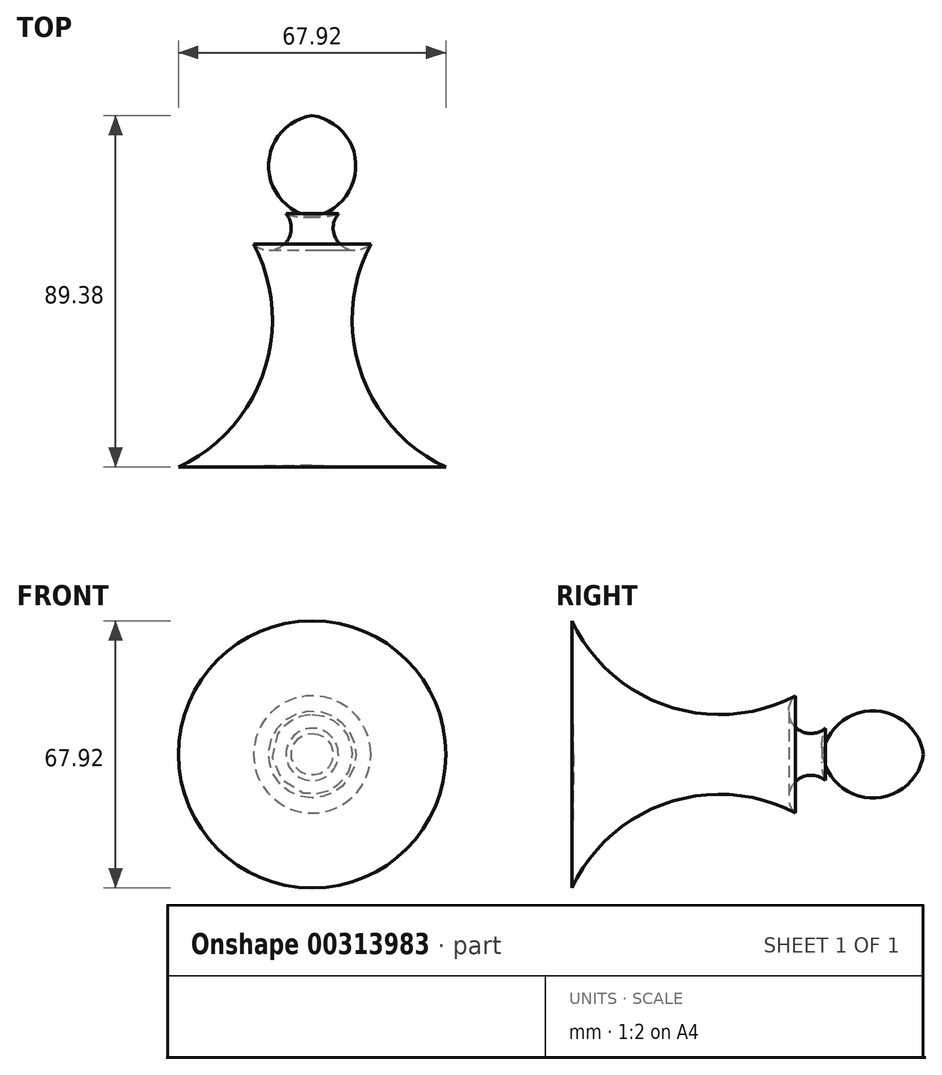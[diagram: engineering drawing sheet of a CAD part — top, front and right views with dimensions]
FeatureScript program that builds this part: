
annotation { "Feature Type Name" : "Feature", "Feature Type Description" : "" }
export const myFeature = defineFeature(function(context is Context, id is Id, definition is map)
    precondition{}
    {
        {
            var Q0;
            Q0=qCreatedBy(makeId("Top.planeOp"),FACE);
            var sketch = newSketch(context, id + "F0", { "sketchPlane" : qUnion([Q0])});
            skLineSegment(sketch, "E0", {"start": v(0, 40.77) * mm, "end": v(0, -48.15) * mm});
            skArc(sketch, "E1", {"start": v(0, 15.05) * mm, "mid": v(14.94, 27.91) * mm, "end": v(0, 40.77) * mm});
            skArc(sketch, "E2", {"start": v(6.65, 15.8) * mm, "mid": v(7.1, 8.02) * mm, "end": v(14.89, 8.14) * mm});
            skArc(sketch, "E3", {"start": v(14.89, 8.14) * mm, "mid": v(12.29, -24.31) * mm, "end": v(33.96, -48.61) * mm});
            skLineSegment(sketch, "E4", {"start": v(0, -48.15) * mm, "end": v(33.96, -48.61) * mm});
            skSolve(sketch);
        }
        {
            var Q0;
            {var subQ0=sQuery(id+"F0.wireOp",EDGE,"E1");var subQ1=sQuery(id+"F0.wireOp",EDGE,"E0");var subQ2=makeQuery(id+"F0.imprint","INTERSECT",VERTEX,{"disambiguationData":[OD(0.0)],"derivedFrom":[subQ1,subQ0]});Q0=makeQuery(id+"F0.imprint","IMPRINT",FACE,{"disambiguationData":[TD([[makeQuery(id+"F0.imprint","IMPRINT",EDGE,{"disambiguationData":[TD([[subQ2,-1.0]])],"derivedFrom":subQ1}),1.0]])]});}
            var Q1;
            {var subQ0=sQuery(id+"F0.wireOp",EDGE,"E2");Q1=makeQuery(id+"F0.imprint","IMPRINT",FACE,{"disambiguationData":[TD([[makeQuery(id+"F0.imprint","IMPRINT",EDGE,{"derivedFrom":subQ0}),-1.0]])]});}
            var Q2;
            Q2=sQuery(id+"F0.wireOp",EDGE,"E0");
            revolve(context, id + "F1", {"entities" : qUnion([Q0, Q1]), "axis" : qUnion([Q2]), "revolveType" : RevolveType.FULL});
        }
    });
